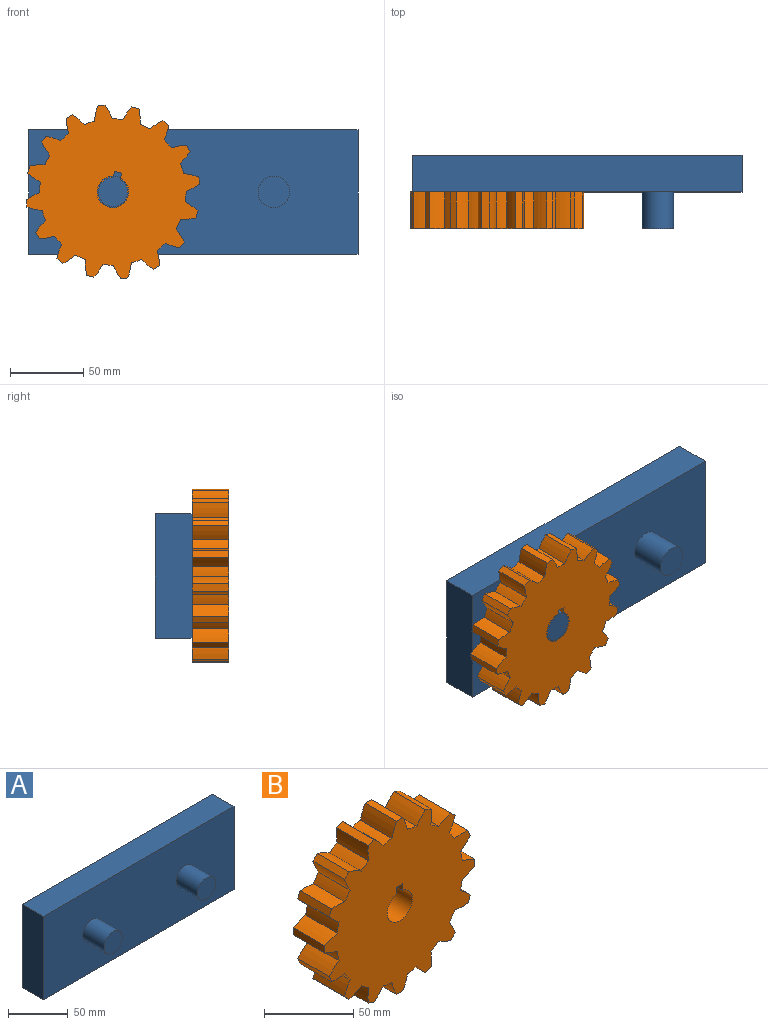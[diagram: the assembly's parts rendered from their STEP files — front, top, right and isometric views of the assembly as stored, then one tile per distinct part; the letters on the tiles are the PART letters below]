
ASSEMBLY  parts=2 mates=1
PART A: 10 faces, bbox 225x50x85 mm
  f0: plane 225x25mm, normal (0,0,-1), area 5625mm2, adj f1,f3,f4,f5
  f1: plane 85x25mm, normal (1,0,0), area 2125mm2, adj f0,f2,f4,f5
  f2: plane 225x25mm, normal (0,0,1), area 5625mm2, adj f1,f3,f4,f5
  f3: plane 85x25mm, normal (-1,0,0), area 2125mm2, adj f0,f2,f4,f5
  f4: plane 225x85mm, normal (0,-1,0), area 18394.5mm2, adj f0,f1,f2,f3,f6,f8
  f5: plane 225x85mm, normal (0,1,0), area 19125mm2, adj f0,f1,f2,f3
  f6: cylinder r=10.78mm len=25mm, axis (0,1,0), area 1693.8mm2, adj f4,f7
  f7: plane 21.57x21.57mm, normal (0,-1,0), area 365.3mm2, adj f6
  f8: cylinder r=10.78mm len=25mm, axis (0,1,0), area 1693.8mm2, adj f4,f9
  f9: plane 21.57x21.57mm, normal (0,-1,0), area 365.3mm2, adj f8
PART B: 70 faces, bbox 119.1x25x119.1 mm
  f0: plane 25x5mm, normal (0,0,-1), area 125mm2, adj f1,f67,f68,f69
  f1: plane 25x4.32mm, normal (-1,0,0), area 107.9mm2, adj f0,f2,f68,f69
  f2: cylinder r=10mm len=25mm, axis (0,1,0), area 1444.5mm2, adj f1,f67,f68,f69
  f3: plane 25x5mm, normal (1,0,0), area 125mm2, adj f4,f66,f68,f69
  f4: cylinder r=44.86mm len=25mm, axis (0,1,0), area 265.5mm2, adj f3,f5,f68,f69
  f5: cylinder r=50mm len=25mm, axis (0,1,0), area 180.7mm2, adj f4,f6,f68,f69
  f6: cylinder r=44.86mm len=25mm, axis (0,1,0), area 265.5mm2, adj f5,f7,f68,f69
  f7: plane 25x4.62mm, normal (0.92,0,0.38), area 125mm2, adj f6,f8,f68,f69
  f8: cylinder r=44.86mm len=25mm, axis (0,1,0), area 265.5mm2, adj f7,f9,f68,f69
  f9: cylinder r=50mm len=25mm, axis (0,1,0), area 180.7mm2, adj f8,f10,f68,f69
  f10: cylinder r=44.86mm len=25mm, axis (0,1,0), area 265.5mm2, adj f9,f11,f68,f69
  f11: plane 25x3.54mm, normal (0.71,0,0.71), area 125mm2, adj f10,f12,f68,f69
  f12: cylinder r=44.86mm len=25mm, axis (0,1,0), area 265.5mm2, adj f11,f13,f68,f69
  f13: cylinder r=50mm len=25mm, axis (0,1,0), area 180.7mm2, adj f12,f14,f68,f69
  f14: cylinder r=44.86mm len=25mm, axis (0,1,0), area 265.5mm2, adj f13,f15,f68,f69
  f15: plane 25x4.62mm, normal (0.38,0,0.92), area 125mm2, adj f14,f16,f68,f69
  f16: cylinder r=44.86mm len=25mm, axis (0,1,0), area 265.5mm2, adj f15,f17,f68,f69
  f17: cylinder r=50mm len=25mm, axis (0,1,0), area 180.7mm2, adj f16,f18,f68,f69
  f18: cylinder r=44.86mm len=25mm, axis (0,1,0), area 265.5mm2, adj f17,f19,f68,f69
  f19: plane 25x5mm, normal (0,0,1), area 125mm2, adj f18,f20,f68,f69
  f20: cylinder r=44.86mm len=25mm, axis (0,1,0), area 265.5mm2, adj f19,f21,f68,f69
  f21: cylinder r=50mm len=25mm, axis (0,1,0), area 180.7mm2, adj f20,f22,f68,f69
  f22: cylinder r=44.86mm len=25mm, axis (0,1,0), area 265.5mm2, adj f21,f23,f68,f69
  f23: plane 25x4.62mm, normal (-0.38,0,0.92), area 125mm2, adj f22,f24,f68,f69
  f24: cylinder r=44.86mm len=25mm, axis (0,1,0), area 265.5mm2, adj f23,f25,f68,f69
  f25: cylinder r=50mm len=25mm, axis (0,1,0), area 180.7mm2, adj f24,f26,f68,f69
  f26: cylinder r=44.86mm len=25mm, axis (0,1,0), area 265.5mm2, adj f25,f27,f68,f69
  f27: plane 25x3.54mm, normal (-0.71,0,0.71), area 125mm2, adj f26,f28,f68,f69
  f28: cylinder r=44.86mm len=25mm, axis (0,1,0), area 265.5mm2, adj f27,f29,f68,f69
  f29: cylinder r=50mm len=25mm, axis (0,1,0), area 180.7mm2, adj f28,f30,f68,f69
  f30: cylinder r=44.86mm len=25mm, axis (0,1,0), area 265.5mm2, adj f29,f31,f68,f69
  f31: plane 25x4.62mm, normal (-0.92,0,0.38), area 125mm2, adj f30,f32,f68,f69
  f32: cylinder r=44.86mm len=25mm, axis (0,1,0), area 265.5mm2, adj f31,f33,f68,f69
  f33: cylinder r=50mm len=25mm, axis (0,1,0), area 180.7mm2, adj f32,f34,f68,f69
  f34: cylinder r=44.86mm len=25mm, axis (0,1,0), area 265.5mm2, adj f33,f35,f68,f69
  f35: plane 25x5mm, normal (-1,0,0), area 125mm2, adj f34,f36,f68,f69
  f36: cylinder r=44.86mm len=25mm, axis (0,1,0), area 265.5mm2, adj f35,f37,f68,f69
  f37: cylinder r=50mm len=25mm, axis (0,1,0), area 180.7mm2, adj f36,f38,f68,f69
  f38: cylinder r=44.86mm len=25mm, axis (0,1,0), area 265.5mm2, adj f37,f39,f68,f69
  f39: plane 25x4.62mm, normal (-0.92,0,-0.38), area 125mm2, adj f38,f40,f68,f69
  f40: cylinder r=44.86mm len=25mm, axis (0,1,0), area 265.5mm2, adj f39,f41,f68,f69
  f41: cylinder r=50mm len=25mm, axis (0,1,0), area 180.7mm2, adj f40,f42,f68,f69
  f42: cylinder r=44.86mm len=25mm, axis (0,1,0), area 265.5mm2, adj f41,f43,f68,f69
  f43: plane 25x3.54mm, normal (-0.71,0,-0.71), area 125mm2, adj f42,f44,f68,f69
  f44: cylinder r=44.86mm len=25mm, axis (0,1,0), area 265.5mm2, adj f43,f45,f68,f69
  f45: cylinder r=50mm len=25mm, axis (0,1,0), area 180.7mm2, adj f44,f46,f68,f69
  f46: cylinder r=44.86mm len=25mm, axis (0,1,0), area 265.5mm2, adj f45,f47,f68,f69
  f47: plane 25x4.62mm, normal (-0.38,0,-0.92), area 125mm2, adj f46,f48,f68,f69
  f48: cylinder r=44.86mm len=25mm, axis (0,1,0), area 265.5mm2, adj f47,f49,f68,f69
  f49: cylinder r=50mm len=25mm, axis (0,1,0), area 180.7mm2, adj f48,f50,f68,f69
  f50: cylinder r=44.86mm len=25mm, axis (0,1,0), area 265.5mm2, adj f49,f51,f68,f69
  f51: plane 25x5mm, normal (0,0,-1), area 125mm2, adj f50,f52,f68,f69
  f52: cylinder r=44.86mm len=25mm, axis (0,1,0), area 265.5mm2, adj f51,f53,f68,f69
  f53: cylinder r=50mm len=25mm, axis (0,1,0), area 180.7mm2, adj f52,f54,f68,f69
  f54: cylinder r=44.86mm len=25mm, axis (0,1,0), area 265.5mm2, adj f53,f55,f68,f69
  f55: plane 25x4.62mm, normal (0.38,0,-0.92), area 125mm2, adj f54,f56,f68,f69
  f56: cylinder r=44.86mm len=25mm, axis (0,1,0), area 265.5mm2, adj f55,f57,f68,f69
  f57: cylinder r=50mm len=25mm, axis (0,1,0), area 180.7mm2, adj f56,f58,f68,f69
  f58: cylinder r=44.86mm len=25mm, axis (0,1,0), area 265.5mm2, adj f57,f59,f68,f69
  f59: plane 25x3.54mm, normal (0.71,0,-0.71), area 125mm2, adj f58,f60,f68,f69
  f60: cylinder r=44.86mm len=25mm, axis (0,1,0), area 265.5mm2, adj f59,f61,f68,f69
  f61: cylinder r=50mm len=25mm, axis (0,1,0), area 180.7mm2, adj f60,f62,f68,f69
  f62: cylinder r=44.86mm len=25mm, axis (0,1,0), area 265.5mm2, adj f61,f63,f68,f69
  f63: plane 25x4.62mm, normal (0.92,0,-0.38), area 125mm2, adj f62,f64,f68,f69
  f64: cylinder r=44.86mm len=25mm, axis (0,1,0), area 265.5mm2, adj f63,f65,f68,f69
  f65: cylinder r=50mm len=25mm, axis (0,1,0), area 180.7mm2, adj f64,f66,f68,f69
  f66: cylinder r=44.86mm len=25mm, axis (0,1,0), area 265.5mm2, adj f3,f65,f68,f69
  f67: plane 25x4.32mm, normal (1,0,0), area 107.9mm2, adj f0,f2,f68,f69
  f68: plane 119.1x119.1mm, normal (0,-1,0), area 8920.1mm2, adj f0,f1,f2,f3,f4,f5,f6,f7
  f69: plane 119.1x119.1mm, normal (0,1,0), area 8920.1mm2, adj f0,f1,f2,f3,f4,f5,f6,f7
PLACE A t=(6.76,2.48,-5.31)mm
PLACE B rot(axis=(0,1,0),14.9deg) t=(205.67,-22.52,4.82)mm
MATE revolute B.f2 <-> A.f6  axis (0,1,0) through (205.67,-22.52,4.82)mm
